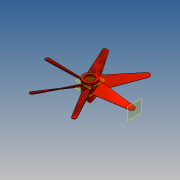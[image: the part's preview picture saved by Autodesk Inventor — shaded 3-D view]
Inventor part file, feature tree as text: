
AUTODESK INVENTOR PART (.ipt)
format: ipt  version: 2015 (Build 190159000, 159)  size: 1,088,000 bytes
history: native  units: mm
features: sketch x5, fillet x4, plane x3, extrude x2, loft x1, pattern_circular x1, revolve x1
ambient origin geometry x8: Origin, YZ Plane, XZ Plane, XY Plane, X Axis, Y Axis, Z Axis, Center Point
bodies: Solid1 (feature_tree)
feature tree (17):
  extrude  "Extrusion1"  Depth=5.0mm TaperAngle=0.0deg
  plane  "Work Plane1"
  plane  "Work Plane2"
  sketch  "Sketch7"  dims[d3=1.5mm d4=-1.5mm d7=5.5mm d8=0.5mm d9=20.0mm]
  plane  "Work Plane3"
  loft  "Loft1"
  fillet  "Fillet1"  Radius=0.5mm
  fillet  "Fillet3"  Radius=20.0mm
  pattern_circular  "Circular Pattern1"  Angle=90.0deg  [1 undecoded]
  extrude  "Extrusion2"  TaperAngle=0.0deg  [1 undecoded]
  fillet  "Fillet4"  Radius=1.0mm
  fillet  "Fillet5"  Radius=0.2mm
  revolve  "Revolution1"  Angle=360.0deg
  sketch  "Sketch1"  dims[d0=6.0mm d1=5.0mm d2=0.0mm]
  sketch  "Sketch9"  dims[d10=45.0deg]
  sketch  "Sketch10"  dims[d11=2.0mm]
  sketch  "Sketch11"  dims[d12=0.3mm d13=0.0mm d14=90.0deg d15=0.0mm d16=90.0deg d17=1.0mm d19=0.2mm d20=60.0mm d21=360.0deg d23=4.0mm d24=5.0mm d25=0.0mm d26=1.745329mm d27=0.2mm d28=0.2mm d30=5.0mm d31=90.0deg d32=0.1mm]
note: 2 required parameter values undecoded (feature->parameter linkage not recoverable at this tier; creation-order binding heuristic only, values carry confidence <= 0.55)
